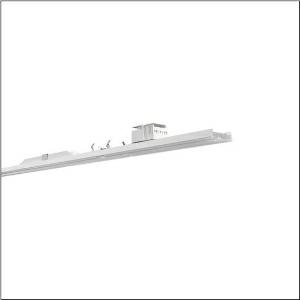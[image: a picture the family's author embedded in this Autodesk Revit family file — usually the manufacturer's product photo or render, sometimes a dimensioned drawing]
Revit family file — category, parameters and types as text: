
# Revit family: licross_r__11_recessed_extreme_ho_51tl11dn4dxre_4439
name_source: partatom
category: Lighting Fixtures
units: mm (PartAtom-declared; Revit-internal decimal feet)

## family parameters
Cut with Voids When Loaded = No
Host = Face
Light Source = No
Part Type = Normal
Room Calculation Point = No
Round Connector Dimension = Use Diameter
Shared = No

## types (1)
- --- (1 x LED, 13060 lm, 76.5 W, 4000K)
    Apparent Load = 77 VA
    CIE Flux Codes = 87 95 99 100 100
    Color Rendering = 80
    Color Temperature = 4000K
    Default Elevation = 1800 mm
    Description = Licross® 11 Recessed extreme HOluminaire insert, length: 1.500mm, width: 66mm, height: 67mm, LED rated luminous flux: 13.060lm, light colour: 840, control gear: DALI 2, control gear: ECG DALI, with plug, 5-pole, with phase selection, mains connection: 220..240V, AC, 50/60Hz, halogen-free wiring, primary optical cover: cover, of PMMA, light emission: direct distribution, protection rating (complete): IP40, insulation class (complete): insulation class I (protective earthing), certification: CE, ENEC, VDE, protection symbol: D if used in an environment without relevant dust loads with corresponding accessories, permissible ambient temperature for indoor applications: -25..+40°C, reducing of maximum allowable ambient temperature of 5°C with ceiling mounting, corresponds to IFS (International Featured Standards) requirements for safety and quality in the food industry, packaging unit: 1 piece
    Height = 58 mm
    Lamp = 1 x LED
    Lamp Light Flux = 13060 lm
    Lamp Power = 76.5 W
    Lamp count = 1
    Length = 1500 mm
    Luminous efficacy = 171 lm/W
    Manufacturer = Siteco
    ModVariant = No
    Model = 51TL11DN4DXRE
    Mounting Place = Ceiling
    Mounting Type = Pendant
    Number of Poles = 1
    OnlyDefault = Yes
    Power Factor = 1
    Product Name = Licross® 11 Recessed extreme HO
    Product group = luminaire insert
    ProductGroupID = 902
    Protection Class = Protection class I
    Protection Degree = IP 40
    RLX_Detail_Level = 1
    RlxData = <blob elided: 22205 chars, md5=f3ec82bf>
    Socket = socket
    Standby Power = 0 W
    System Light Flux = 13060 lm
    System Power = 77 W
    Type Comments = factory setting: luminous flux: 100 % | dim-lin: 254 | 435 mA
    Type Image = l_1266722.jpg
    URL = http://relux.com
    VarID = @adj_132474
    Voltage = 0 V
    Weight = 0.00 kg
    Width = 66 mm

## geometry (parser evidence)
native form markers: Blend x4, Sweep x11
no freeform markers — native parametric forms only
